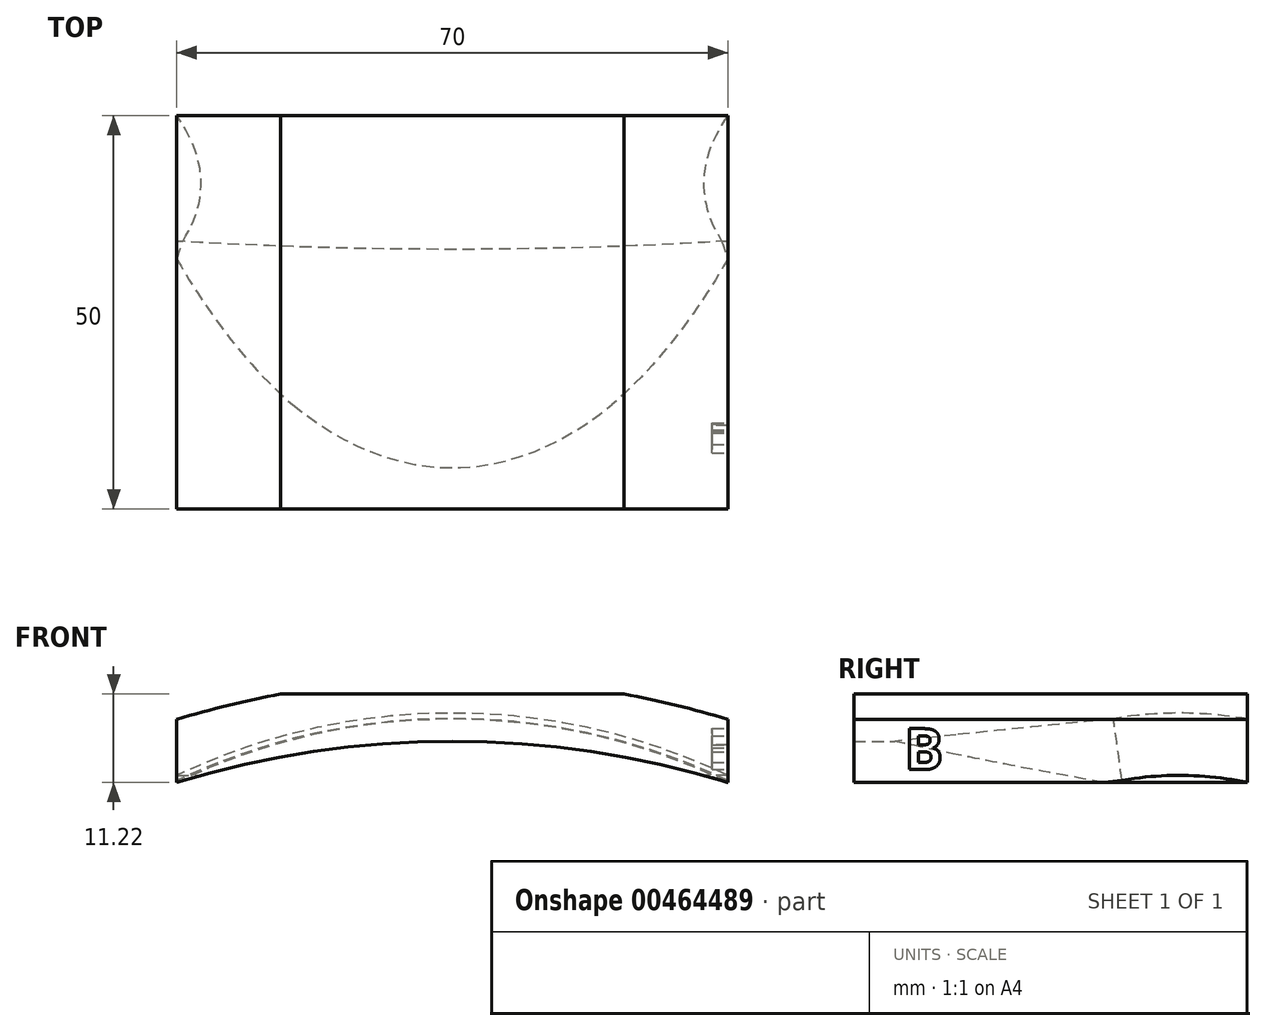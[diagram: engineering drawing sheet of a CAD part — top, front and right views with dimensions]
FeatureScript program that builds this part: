
annotation { "Feature Type Name" : "Feature", "Feature Type Description" : "" }
export const myFeature = defineFeature(function(context is Context, id is Id, definition is map)
    precondition{}
    {
        {
            var Q0;
            Q0=qCreatedBy(makeId("Front.planeOp"),FACE);
            var sketch = newSketch(context, id + "F0", { "sketchPlane" : qUnion([Q0])});
            skArc(sketch, "E0", {"start": v(70, 0) * mm, "mid": v(35, 5.22) * mm, "end": v(0, 0) * mm});
            skLineSegment(sketch, "E1", {"start": v(0, 0) * mm, "end": v(0, 8) * mm});
            skLineSegment(sketch, "E2", {"start": v(13.18, 11.22) * mm, "end": v(56.82, 11.22) * mm});
            skLineSegment(sketch, "E3", {"start": v(70, 8) * mm, "end": v(70, 0) * mm});
            skArc(sketch, "E4", {"start": v(70, 8) * mm, "mid": v(63.45, 9.8) * mm, "end": v(56.82, 11.22) * mm});
            skPoint(sketch, "E5.orphan", {"position": v(70, 11.22) * mm});
            skArc(sketch, "E6.trimOffspring", {"start": v(13.18, 11.22) * mm, "mid": v(6.55, 9.8) * mm, "end": v(0, 8) * mm});
            skSolve(sketch);
        }
        {
            var Q0;
            Q0=qSketchRegion(id+"F0",true);
            extrude(context, id + "F1", {"entities" : qUnion([Q0]), "depth" : 25 * mm, "hasSecondDirection" : true, "secondDirectionOppositeDirection" : true, "secondDirectionDepth" : 25 * mm});
        }
        {
            var Q0;
            Q0=qCreatedBy(makeId("Right.planeOp"),FACE);
            cPlane(context, id + "F2", {"entities" : qUnion([Q0]), "cplaneType" : CPlaneType.OFFSET, "offset" : 35 * mm, "width" : 150 * mm, "height" : 150 * mm});
        }
        {
            var Q0;
            Q0=qCreatedBy(id+"F2.planeOp",FACE);
            var sketch = newSketch(context, id + "F3", { "sketchPlane" : qUnion([Q0])});
            skLineSegment(sketch, "E7", {"start": v(-29.46, 6) * mm, "end": v(30.4, 6) * mm, "construction": true});
            skLineSegment(sketch, "E8", {"start": v(25, 10.7) * mm, "end": v(25, 0) * mm, "construction": true});
            skArc(sketch, "E9", {"start": v(25, 8) * mm, "mid": v(16.5, 8.75) * mm, "end": v(8, 8.05) * mm});
            skPoint(sketch, "E9.endSnap0", {"position": v(0.47, 6) * mm});
            skLineSegment(sketch, "E10", {"start": v(8, 8.05) * mm, "end": v(-12, 6) * mm});
            skPoint(sketch, "E11.orphan", {"position": v(0, 6) * mm});
            skLineSegment(sketch, "E12", {"start": v(-12, 6) * mm, "end": v(-40, 3) * mm});
            skSolve(sketch);
        }
        {
            var Q0;
            Q0=makeQuery(id+"F1.opExtrude","CAP_FACE",FACE,{"disambiguationData":[OSD([sQuery(id+"F0.wireOp",EDGE,"E0"),sQuery(id+"F0.wireOp",EDGE,"E1"),sQuery(id+"F0.wireOp",EDGE,"E2"),sQuery(id+"F0.wireOp",EDGE,"E3"),sQuery(id+"F0.wireOp",EDGE,"E4"),sQuery(id+"F0.wireOp",EDGE,"E6.trimOffspring")])],"isStart":true});
            var sketch = newSketch(context, id + "F4", { "sketchPlane" : qUnion([Q0])});
            skArc(sketch, "E13", {"start": v(0, 0) * mm, "mid": v(-35, 8.05) * mm, "end": v(-70, 0) * mm});
            skLineSegment(sketch, "E14", {"start": v(-70, 0) * mm, "end": v(0, 0) * mm});
            skSolve(sketch);
        }
        {
            var Q0;
            Q0=makeQuery(id+"F4.imprint","IMPRINT",FACE,{"disambiguationData":[TD([[makeQuery(id+"F4.imprint","IMPRINT",EDGE,{"derivedFrom":sQuery(id+"F4.wireOp",EDGE,"E14")}),1.0]])]});
            var Q1;
            Q1=makeQuery(id+"F4.imprint","IMPRINT",FACE,{"disambiguationData":[TD([[makeQuery(id+"F4.imprint","IMPRINT",EDGE,{"derivedFrom":sQuery(id+"F4.wireOp",EDGE,"E13")}),1.0]])]});
            var Q2;
            Q2=sQuery(id+"F3.wireOp",EDGE,"E9");
            var Q3;
            Q3=sQuery(id+"F3.wireOp",EDGE,"E10");
            var Q4;
            Q4=sQuery(id+"F3.wireOp",EDGE,"E12");
            sweep(context, id + "F5", {"operationType" : NewBodyOperationType.REMOVE, "profiles" : qUnion([Q0, Q1]), "path" : qUnion([Q2, Q3, Q4])});
        }
        {
            var Q0;
            {var subQ1=sQuery(id+"F0.wireOp",EDGE,"E4");var subQ2=sQuery(id+"F0.wireOp",EDGE,"E3");Q0=makeQuery(id+"F5.boolean.opBoolean","SPLIT",FACE,{"disambiguationData":[TD([makeQuery(id+"F1.opExtrude","SWEPT_FACE",FACE,{"disambiguationData":[OSD([subQ1])]})])],"derivedFrom":makeQuery(id+"F1.opExtrude","SWEPT_FACE",FACE,{"disambiguationData":[OSD([subQ2])]})});}
            var sketch = newSketch(context, id + "F6", { "sketchPlane" : qUnion([Q0])});
            skText(sketch, "E15", { "text": "B", "fontName": "OpenSans-Bold.ttf"});
            const initialGuessF6  = {"E15": [-0.01856, 0.00162, 1, 0, 0.00526]};
            skSetInitialGuess(sketch, initialGuessF6);
            skSolve(sketch);
        }
        {
            var Q0;
            Q0 = qSketchRegion(id + "F6", true);
            extrude(context, id + "F7", {"entities" : qUnion([Q0]), "operationType" : NewBodyOperationType.REMOVE, "oppositeDirection" : true, "depth" : 2 * mm});
        }
    });
